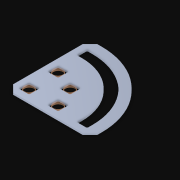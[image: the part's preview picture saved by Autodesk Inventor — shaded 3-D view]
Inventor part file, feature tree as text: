
AUTODESK INVENTOR PART (.ipt)
format: ipt  version: 2021 (Build 250183000, 183)  size: 206,336 bytes
history: native  units: in
note: dims shown in document units (in); Inventor stores cm internally (conversion verified against a paired STEP export)
features: other x5, extrude x4, sketch x2, imported_body x1, pattern_linear x1
ambient origin geometry x8: Origin, YZ Plane, XZ Plane, XY Plane, X Axis, Y Axis, Z Axis, Center Point
bodies: Body1 (feature_tree), Body2 (feature_tree), Body3 (feature_tree), Body4 (feature_tree), Body5 (feature_tree)
feature tree (13):
  parser-record x1  (decoder bookkeeping rows leaked as tree rows — omitted from the tree; the rows remain in map.json)
  imported_body  "Base1"
  pattern_linear  "Rectangular Pattern1"  Count1=2 Spacing1=0.5in
  other  "Srf1"
  other  "Srf2"
  sketch  "Sketch2"  dims[d1=0.046in d2=0.0in d3=0.7874in d5=0.5in]
  other  "Srf3"
  sketch  "Sketch3"  dims[d7=0.046in d8=0.0in d10=0.046in d11=0.0in]
  other  "Srf4"
  extrude  "ExtrusionSrf1"  Depth=0.046in TaperAngle=0.0deg
  extrude  "ExtrusionSrf3"  [1 undecoded]
  extrude  "ExtrusionSrf4"  [1 undecoded]
  extrude  "ExtrusionSrf2"  [1 undecoded]
note: 3 required parameter values undecoded (feature->parameter linkage not recoverable at this tier; creation-order binding heuristic only, values carry confidence <= 0.55)
